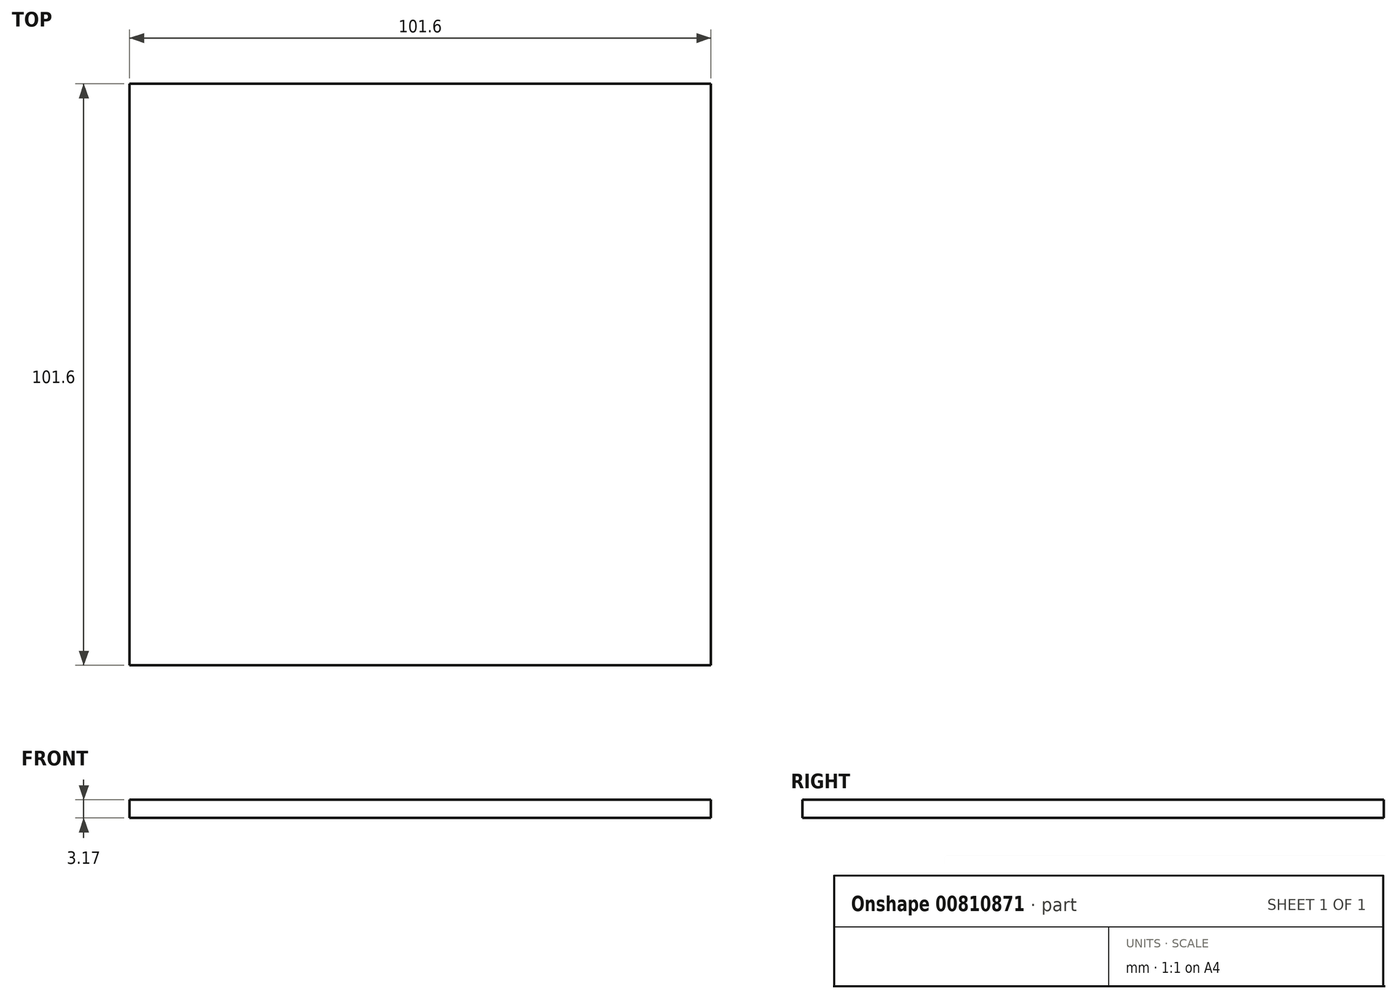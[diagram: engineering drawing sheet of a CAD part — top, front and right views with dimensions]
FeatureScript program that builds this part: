
annotation { "Feature Type Name" : "Feature", "Feature Type Description" : "" }
export const myFeature = defineFeature(function(context is Context, id is Id, definition is map)
    precondition{}
    {
        {
            var Q0;
            Q0=qCreatedBy(makeId("Top.planeOp"),FACE);
            var sketch = newSketch(context, id + "F0", { "sketchPlane" : qUnion([Q0])});
            skLineSegment(sketch, "E0.bottom", {"start": v(-52.16, -41.23) * mm, "end": v(49.44, -41.23) * mm});
            skLineSegment(sketch, "E0.top", {"start": v(-52.16, 60.37) * mm, "end": v(49.44, 60.37) * mm});
            skLineSegment(sketch, "E0.left", {"start": v(-52.16, -41.23) * mm, "end": v(-52.16, 60.37) * mm});
            skLineSegment(sketch, "E0.right", {"start": v(49.44, -41.23) * mm, "end": v(49.44, 60.37) * mm});
            skSolve(sketch);
        }
        {
            var Q0;
            Q0 = qSketchRegion(id + "F0", true);
            extrude(context, id + "F1", {"entities" : qUnion([Q0]), "depth" : 3.17 * mm, "offsetDistance" : 25.4 * mm});
        }
    });
